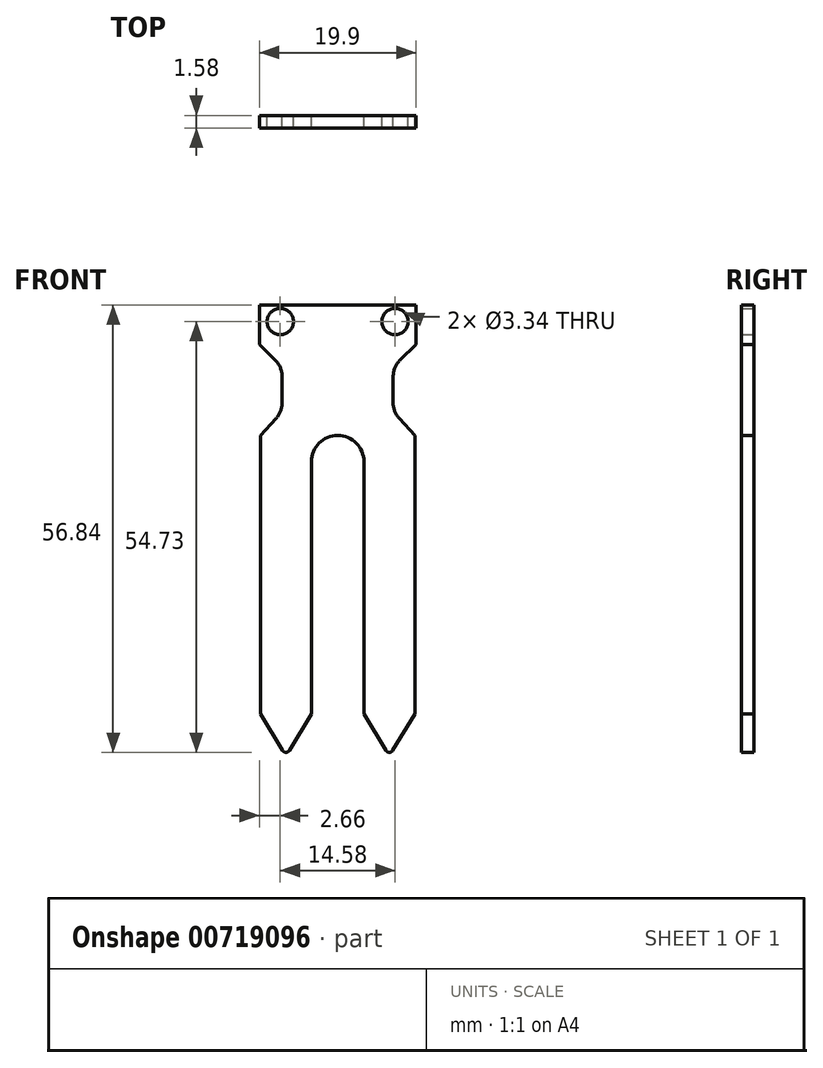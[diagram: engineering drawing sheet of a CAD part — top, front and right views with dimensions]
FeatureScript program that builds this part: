
annotation { "Feature Type Name" : "Feature", "Feature Type Description" : "" }
export const myFeature = defineFeature(function(context is Context, id is Id, definition is map)
    precondition{}
    {
        {
            var Q0;
            Q0=qCreatedBy(makeId("Front.planeOp"),FACE);
            var sketch = newSketch(context, id + "F0", { "sketchPlane" : qUnion([Q0])});
            skLineSegment(sketch, "E0", {"start": v(-9.95, 0) * mm, "end": v(9.95, 0) * mm});
            skLineSegment(sketch, "E1", {"start": v(-9.95, 0) * mm, "end": v(-9.95, -5) * mm});
            skLineSegment(sketch, "E2", {"start": v(9.95, 0) * mm, "end": v(9.95, -5) * mm});
            skLineSegment(sketch, "E3", {"start": v(-9.95, -5) * mm, "end": v(-7.05, -7.87) * mm});
            skLineSegment(sketch, "E4", {"start": v(9.95, -5) * mm, "end": v(7.05, -7.87) * mm});
            skLineSegment(sketch, "E5", {"start": v(-7.05, -7.87) * mm, "end": v(-7.05, -13.57) * mm});
            skLineSegment(sketch, "E6", {"start": v(7.05, -7.87) * mm, "end": v(7.05, -13.57) * mm});
            skLineSegment(sketch, "E7", {"start": v(-7.05, -13.57) * mm, "end": v(-9.8, -16.58) * mm});
            skLineSegment(sketch, "E8", {"start": v(7.05, -13.57) * mm, "end": v(9.8, -16.58) * mm});
            skLineSegment(sketch, "E9", {"start": v(-9.8, -16.58) * mm, "end": v(-9.8, -51.98) * mm});
            skLineSegment(sketch, "E10", {"start": v(9.8, -16.58) * mm, "end": v(9.8, -51.98) * mm});
            skLineSegment(sketch, "E11", {"start": v(-9.8, -51.98) * mm, "end": v(-6.57, -57.3) * mm});
            skLineSegment(sketch, "E12", {"start": v(-6.57, -57.3) * mm, "end": v(-3.33, -51.98) * mm});
            skLineSegment(sketch, "E13", {"start": v(-3.33, -51.98) * mm, "end": v(-3.33, -19.91) * mm});
            skLineSegment(sketch, "E14", {"start": v(9.8, -51.98) * mm, "end": v(6.57, -57.3) * mm});
            skLineSegment(sketch, "E15", {"start": v(6.57, -57.3) * mm, "end": v(3.34, -51.98) * mm});
            skLineSegment(sketch, "E16", {"start": v(3.33, -51.98) * mm, "end": v(3.33, -19.91) * mm});
            skArc(sketch, "E17", {"start": v(3.33, -19.91) * mm, "mid": v(0, -16.58) * mm, "end": v(-3.33, -19.91) * mm});
            skCircle(sketch, "E18", {"center": v(-7.3, -2.1) * mm, "radius": 1.67 * mm});
            skPoint(sketch, "E19", {"position": v(0, -16.58) * mm});
            skLineSegment(sketch, "E20", {"start": v(0, 0) * mm, "end": v(0, -16.58) * mm, "construction": true});
            skCircle(sketch, "E21.MirrorC", {"center": v(7.3, -2.1) * mm, "radius": 1.67 * mm});
            skSolve(sketch);
        }
        {
            var Q0;
            Q0=makeQuery(id+"F0.imprint","IMPRINT",FACE,{"disambiguationData":[TD([[makeQuery(id+"F0.imprint","IMPRINT",EDGE,{"derivedFrom":sQuery(id+"F0.wireOp",EDGE,"E0")}),-1.0]])]});
            extrude(context, id + "F1", {"entities" : qUnion([Q0]), "depth" : 1.58 * mm, "offsetDistance" : 25 * mm});
        }
        {
            var Q0;
            Q0=makeQuery(id+"F1.opExtrude","SWEPT_EDGE",EDGE,{"disambiguationData":[OSD([sQuery(id+"F0.wireOp",EDGE,"E3"),sQuery(id+"F0.wireOp",EDGE,"E5")])]});
            var Q1;
            Q1=makeQuery(id+"F1.opExtrude","SWEPT_EDGE",EDGE,{"disambiguationData":[OSD([sQuery(id+"F0.wireOp",EDGE,"E5"),sQuery(id+"F0.wireOp",EDGE,"E7")])]});
            var Q2;
            Q2=makeQuery(id+"F1.opExtrude","SWEPT_EDGE",EDGE,{"disambiguationData":[OSD([sQuery(id+"F0.wireOp",EDGE,"E4"),sQuery(id+"F0.wireOp",EDGE,"E6")])]});
            var Q3;
            Q3=makeQuery(id+"F1.opExtrude","SWEPT_EDGE",EDGE,{"disambiguationData":[OSD([sQuery(id+"F0.wireOp",EDGE,"E6"),sQuery(id+"F0.wireOp",EDGE,"E8")])]});
            fillet(context, id + "F2", {"entities" : qUnion([Q0, Q1, Q2, Q3]), "radius" : 3 * mm, "tangentPropagation" : true, "allowEdgeOverflow" : false});
        }
        {
            var Q0;
            Q0=makeQuery(id+"F1.opExtrude","SWEPT_EDGE",EDGE,{"disambiguationData":[OSD([sQuery(id+"F0.wireOp",EDGE,"E11"),sQuery(id+"F0.wireOp",EDGE,"E12")])]});
            var Q1;
            Q1=makeQuery(id+"F1.opExtrude","SWEPT_EDGE",EDGE,{"disambiguationData":[OSD([sQuery(id+"F0.wireOp",EDGE,"E14"),sQuery(id+"F0.wireOp",EDGE,"E15")])]});
            fillet(context, id + "F3", {"entities" : qUnion([Q0, Q1]), "radius" : 0.5 * mm, "tangentPropagation" : true, "allowEdgeOverflow" : false});
        }
    });
